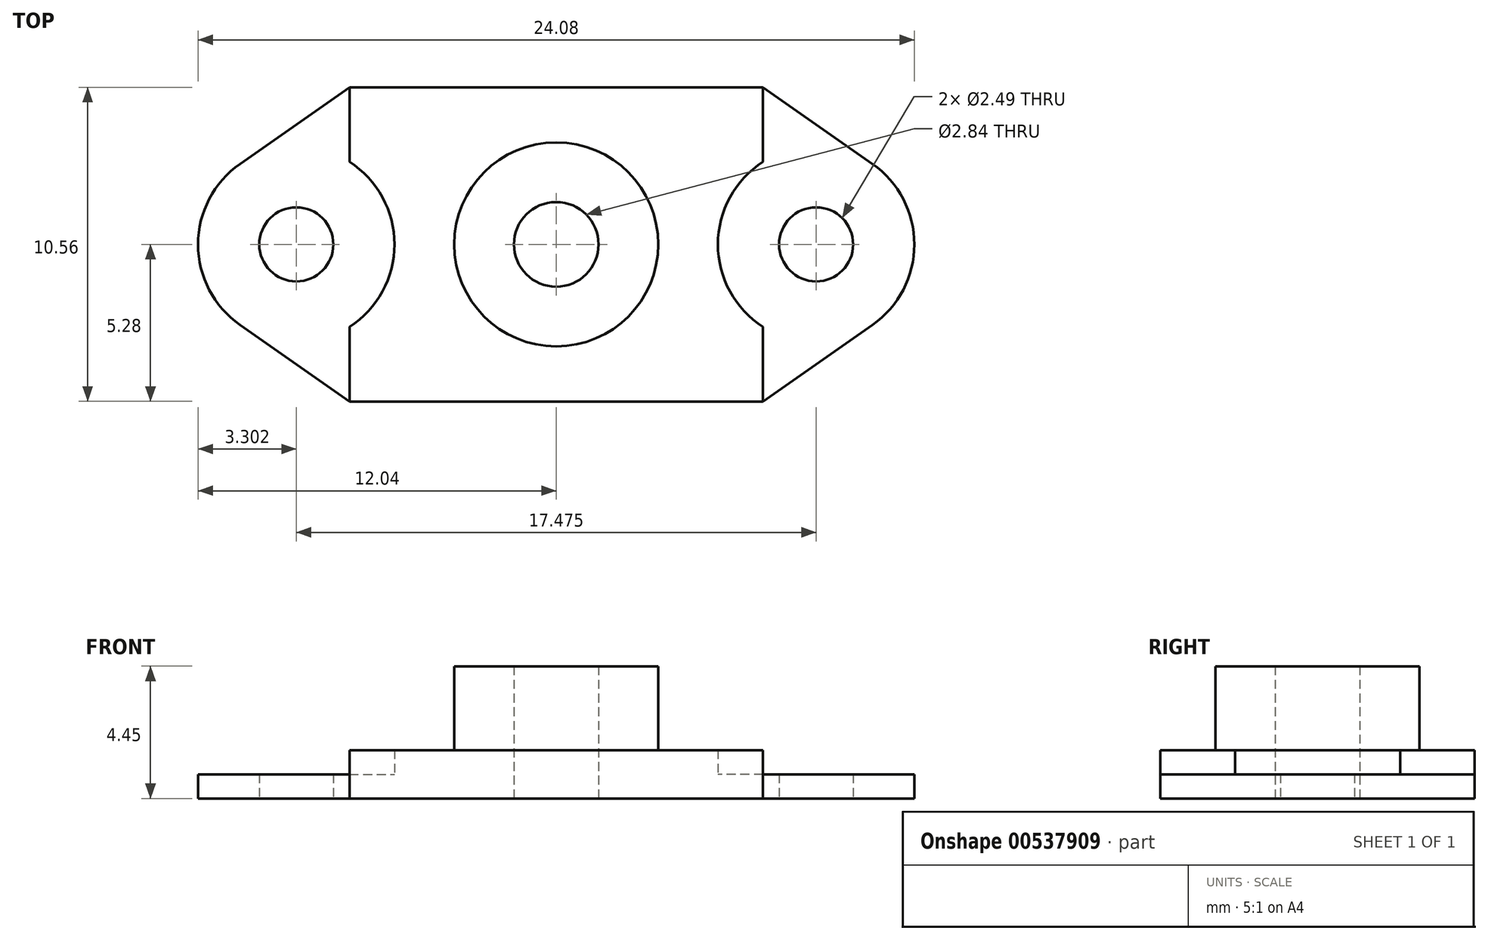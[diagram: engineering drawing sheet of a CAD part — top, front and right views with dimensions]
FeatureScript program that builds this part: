
annotation { "Feature Type Name" : "Feature", "Feature Type Description" : "" }
export const myFeature = defineFeature(function(context is Context, id is Id, definition is map)
    precondition{}
    {
        {
            assignVariable(context, id + "F0", {"variableType" : VariableType.LENGTH, "name" : "H", "lengthValue" : 4.44 * mm});
        }
        {
            assignVariable(context, id + "F1", {"variableType" : VariableType.LENGTH, "name" : "K", "lengthValue" : 2.5 * mm});
        }
        {
            assignVariable(context, id + "F2", {"variableType" : VariableType.LENGTH, "name" : "T", "lengthValue" : 2.84 * mm});
        }
        {
            assignVariable(context, id + "F3", {"variableType" : VariableType.LENGTH, "name" : "V", "lengthValue" : 0.81 * mm});
        }
        {
            var Q0;
            Q0=qCreatedBy(makeId("Top.planeOp"),FACE);
            var sketch = newSketch(context, id + "F4", { "sketchPlane" : qUnion([Q0])});
            skCircle(sketch, "E0", {"center": v(0, 0) * mm, "radius": 3.43 * mm});
            skSolve(sketch);
        }
        {
            var Q0;
            Q0 = qSketchRegion(id + "F4", true);
            var Q1;
            Q1=sQuery(id+"F4.wireOp",EDGE,"E0");
            extrude(context, id + "F5", {"entities" : qUnion([Q0]), "flatOperationType" : FlatOperationType.REMOVE, "surfaceEntities" : qUnion([Q1]), "depth" : getVariable(context, 'H'), "offsetDistance" : 25.4 * mm, "domain" : OperationDomain.MODEL});
        }
        {
            var Q0;
            Q0=qCreatedBy(makeId("Top.planeOp"),FACE);
            var sketch = newSketch(context, id + "F6", { "sketchPlane" : qUnion([Q0])});
            skLineSegment(sketch, "E1", {"start": v(0, 0) * mm, "end": v(0, 5.28) * mm, "construction": true});
            skLineSegment(sketch, "E2", {"start": v(0, 0) * mm, "end": v(8.74, 0) * mm, "construction": true});
            skArc(sketch, "E3", {"start": v(12.04, 0) * mm, "mid": v(11.67, 1.52) * mm, "end": v(10.63, 2.7) * mm});
            skLineSegment(sketch, "E4", {"start": v(0, 5.28) * mm, "end": v(6.95, 5.28) * mm});
            skLineSegment(sketch, "E5", {"start": v(6.95, 5.28) * mm, "end": v(10.63, 2.7) * mm});
            skCircle(sketch, "E6", {"center": v(8.74, 0) * mm, "radius": 1.24 * mm, "construction": true});
            skArc(sketch, "E7.MirrorCS", {"start": v(12.04, 0) * mm, "mid": v(11.67, -1.52) * mm, "end": v(10.63, -2.7) * mm});
            skLineSegment(sketch, "E8.MirrorCS", {"start": v(6.95, -5.28) * mm, "end": v(10.63, -2.7) * mm});
            skLineSegment(sketch, "E9.MirrorCS", {"start": v(0, -5.28) * mm, "end": v(6.95, -5.28) * mm});
            skLineSegment(sketch, "E10.MirrorCS", {"start": v(0, 0) * mm, "end": v(-8.74, 0) * mm, "construction": true});
            skLineSegment(sketch, "E11.MirrorCS", {"start": v(-6.95, -5.28) * mm, "end": v(-10.63, -2.7) * mm});
            skLineSegment(sketch, "E12.MirrorCS", {"start": v(0, -5.28) * mm, "end": v(-6.95, -5.28) * mm});
            skCircle(sketch, "E13.MirrorC", {"center": v(-8.74, 0) * mm, "radius": 1.24 * mm, "construction": true});
            skArc(sketch, "E14.MirrorCS", {"start": v(-12.04, 0) * mm, "mid": v(-11.67, 1.52) * mm, "end": v(-10.63, 2.7) * mm});
            skLineSegment(sketch, "E15.MirrorCS", {"start": v(0, 5.28) * mm, "end": v(-6.95, 5.28) * mm});
            skLineSegment(sketch, "E16.MirrorCS", {"start": v(-6.95, 5.28) * mm, "end": v(-10.63, 2.7) * mm});
            skArc(sketch, "E17.MirrorCS", {"start": v(-12.04, 0) * mm, "mid": v(-11.67, -1.52) * mm, "end": v(-10.63, -2.7) * mm});
            skSolve(sketch);
        }
        {
            var Q0;
            Q0 = qSketchRegion(id + "F6", true);
            extrude(context, id + "F7", {"entities" : qUnion([Q0]), "operationType" : NewBodyOperationType.ADD, "flatOperationType" : FlatOperationType.REMOVE, "depth" : getVariable(context, 'V'), "offsetDistance" : 25.4 * mm, "domain" : OperationDomain.MODEL});
        }
        {
            var Q0;
            Q0=makeQuery(id+"F7.opExtrude","CAP_FACE",FACE,{"disambiguationData":[OSD([sQuery(id+"F6.wireOp",EDGE,"E3"),sQuery(id+"F6.wireOp",EDGE,"E4"),sQuery(id+"F6.wireOp",EDGE,"E5"),sQuery(id+"F6.wireOp",EDGE,"E7.MirrorCS"),sQuery(id+"F6.wireOp",EDGE,"E8.MirrorCS"),sQuery(id+"F6.wireOp",EDGE,"E9.MirrorCS"),sQuery(id+"F6.wireOp",EDGE,"E11.MirrorCS"),sQuery(id+"F6.wireOp",EDGE,"E12.MirrorCS"),sQuery(id+"F6.wireOp",EDGE,"E14.MirrorCS"),sQuery(id+"F6.wireOp",EDGE,"E15.MirrorCS"),sQuery(id+"F6.wireOp",EDGE,"E16.MirrorCS"),sQuery(id+"F6.wireOp",EDGE,"E17.MirrorCS")])],"isStart":false});
            var sketch = newSketch(context, id + "F8", { "sketchPlane" : qUnion([Q0])});
            skLineSegment(sketch, "E18.bottom", {"start": v(-6.95, -5.28) * mm, "end": v(6.95, -5.28) * mm});
            skLineSegment(sketch, "E18.top", {"start": v(-6.95, 5.28) * mm, "end": v(6.95, 5.28) * mm});
            skLineSegment(sketch, "E18.left", {"start": v(-6.95, -5.28) * mm, "end": v(-6.95, 5.28) * mm});
            skLineSegment(sketch, "E18.right", {"start": v(6.95, -5.28) * mm, "end": v(6.95, 5.28) * mm});
            skSolve(sketch);
        }
        {
            var Q0;
            Q0 = qSketchRegion(id + "F8", true);
            extrude(context, id + "F9", {"entities" : qUnion([Q0]), "operationType" : NewBodyOperationType.ADD, "flatOperationType" : FlatOperationType.REMOVE, "depth" : getVariable(context, 'V'), "offsetDistance" : 25.4 * mm, "domain" : OperationDomain.MODEL});
        }
        {
            var Q0;
            {var subQ0=sQuery(id+"F6.wireOp",EDGE,"E8.MirrorCS");var subQ1=sQuery(id+"F6.wireOp",EDGE,"E5");var subQ2=sQuery(id+"F6.wireOp",EDGE,"E15.MirrorCS");var subQ3=sQuery(id+"F6.wireOp",EDGE,"E4");var subQ4=sQuery(id+"F6.wireOp",EDGE,"E7.MirrorCS");var subQ5=sQuery(id+"F6.wireOp",EDGE,"E3");var subQ6=sQuery(id+"F6.wireOp",EDGE,"E12.MirrorCS");var subQ7=sQuery(id+"F6.wireOp",EDGE,"E9.MirrorCS");Q0=makeQuery(id+"F9.boolean.opBoolean","SPLIT",FACE,{"disambiguationData":[TD([makeQuery(id+"F7.opExtrude","SWEPT_FACE",FACE,{"disambiguationData":[OSD([subQ1])]})])],"derivedFrom":makeQuery(id+"F7.opExtrude","CAP_FACE",FACE,{"disambiguationData":[OSD([subQ5,subQ3,subQ1,subQ4,subQ0,subQ7,sQuery(id+"F6.wireOp",EDGE,"E11.MirrorCS"),subQ6,sQuery(id+"F6.wireOp",EDGE,"E14.MirrorCS"),subQ2,sQuery(id+"F6.wireOp",EDGE,"E16.MirrorCS"),sQuery(id+"F6.wireOp",EDGE,"E17.MirrorCS")])],"isStart":false})});}
            var sketch = newSketch(context, id + "F10", { "sketchPlane" : qUnion([Q0])});
            skCircle(sketch, "E19", {"center": v(8.74, 0) * mm, "radius": 3.3 * mm});
            skCircle(sketch, "E20", {"center": v(-8.74, 0) * mm, "radius": 3.3 * mm});
            skSolve(sketch);
        }
        {
            var Q0;
            Q0 = qSketchRegion(id + "F10", true);
            var Q1;
            Q1=makeQuery(id+"F9.opExtrude","CAP_FACE",FACE,{"disambiguationData":[OSD([sQuery(id+"F8.wireOp",EDGE,"E18.bottom"),sQuery(id+"F8.wireOp",EDGE,"E18.top"),sQuery(id+"F8.wireOp",EDGE,"E18.left"),sQuery(id+"F8.wireOp",EDGE,"E18.right")])],"isStart":false});
            extrude(context, id + "F11", {"entities" : qUnion([Q0]), "operationType" : NewBodyOperationType.REMOVE, "endBound" : BoundingType.UP_TO_SURFACE, "depth" : 25.4 * mm, "endBoundEntityFace" : qUnion([Q1]), "offsetDistance" : 25.4 * mm});
        }
        {
            var Q0;
            Q0=makeQuery(id+"F5.opExtrude","CAP_FACE",FACE,{"disambiguationData":[OSD([sQuery(id+"F4.wireOp",EDGE,"E0")])],"isStart":false});
            var sketch = newSketch(context, id + "F12", { "sketchPlane" : qUnion([Q0])});
            skPoint(sketch, "E21", {"position": v(0, 0) * mm});
            skSolve(sketch);
        }
        {
            var Q0;
            Q0=sQuery(id+"F12.wireOp",VERTEX,"E21");
            var Q1;
            Q1=makeQuery(id+"F5.opExtrude","SWEPT_BODY",BODY,{"disambiguationData":[OSD([sQuery(id+"F4.wireOp",EDGE,"E0")])]});
            hole(context, id + "F13", {"style" : HoleStyle.SIMPLE, "endStyle" : HoleEndStyle.THROUGH, "holeDiameter" : getVariable(context, 'T'), "isTappedThrough" : true, "tappedDepth" : 12.7 * mm, "tapClearance" : 3, "locations" : qUnion([Q0]), "scope" : qUnion([Q1]), "majorDiameter" : 4.83 * mm, "startStyle" : HoleStartStyle.PART});
        }
        {
            var Q0;
            {var subQ0=sQuery(id+"F6.wireOp",EDGE,"E11.MirrorCS");var subQ1=sQuery(id+"F6.wireOp",EDGE,"E12.MirrorCS");var subQ2=sQuery(id+"F6.wireOp",EDGE,"E9.MirrorCS");var subQ3=sQuery(id+"F6.wireOp",EDGE,"E17.MirrorCS");var subQ4=sQuery(id+"F6.wireOp",EDGE,"E14.MirrorCS");var subQ5=sQuery(id+"F6.wireOp",EDGE,"E15.MirrorCS");var subQ6=sQuery(id+"F6.wireOp",EDGE,"E4");var subQ7=sQuery(id+"F6.wireOp",EDGE,"E16.MirrorCS");Q0=makeQuery(id+"F11.boolean.opBoolean","MERGE",FACE,{"derivedFrom":[makeQuery(id+"F9.boolean.opBoolean","SPLIT",FACE,{"disambiguationData":[TD([makeQuery(id+"F7.opExtrude","SWEPT_FACE",FACE,{"disambiguationData":[OSD([subQ0])]})])],"derivedFrom":makeQuery(id+"F7.opExtrude","CAP_FACE",FACE,{"disambiguationData":[OSD([sQuery(id+"F6.wireOp",EDGE,"E3"),subQ6,sQuery(id+"F6.wireOp",EDGE,"E5"),sQuery(id+"F6.wireOp",EDGE,"E7.MirrorCS"),sQuery(id+"F6.wireOp",EDGE,"E8.MirrorCS"),subQ2,subQ0,subQ1,subQ4,subQ5,subQ7,subQ3])],"isStart":false})}),makeQuery(id+"F11.opExtrude","CAP_FACE",FACE,{"disambiguationData":[OSD([sQuery(id+"F10.wireOp",EDGE,"E20")])],"isStart":true})]});}
            var sketch = newSketch(context, id + "F14", { "sketchPlane" : qUnion([Q0])});
            skPoint(sketch, "E22", {"position": v(8.74, 0) * mm});
            skPoint(sketch, "E23", {"position": v(-8.74, 0) * mm});
            skSolve(sketch);
        }
        {
            var Q0;
            Q0=sQuery(id+"F14.wireOp",VERTEX,"E23");
            var Q1;
            Q1=sQuery(id+"F14.wireOp",VERTEX,"E22");
            var Q2;
            Q2=makeQuery(id+"F5.opExtrude","SWEPT_BODY",BODY,{"disambiguationData":[OSD([sQuery(id+"F4.wireOp",EDGE,"E0")])]});
            hole(context, id + "F15", {"style" : HoleStyle.SIMPLE, "endStyle" : HoleEndStyle.THROUGH, "holeDiameter" : getVariable(context, 'K'), "majorDiameter" : 6.35 * mm, "isTappedThrough" : true, "tappedDepth" : 12.7 * mm, "tapClearance" : 3, "locations" : qUnion([Q0, Q1]), "scope" : qUnion([Q2]), "startStyle" : HoleStartStyle.PART});
        }
    });
